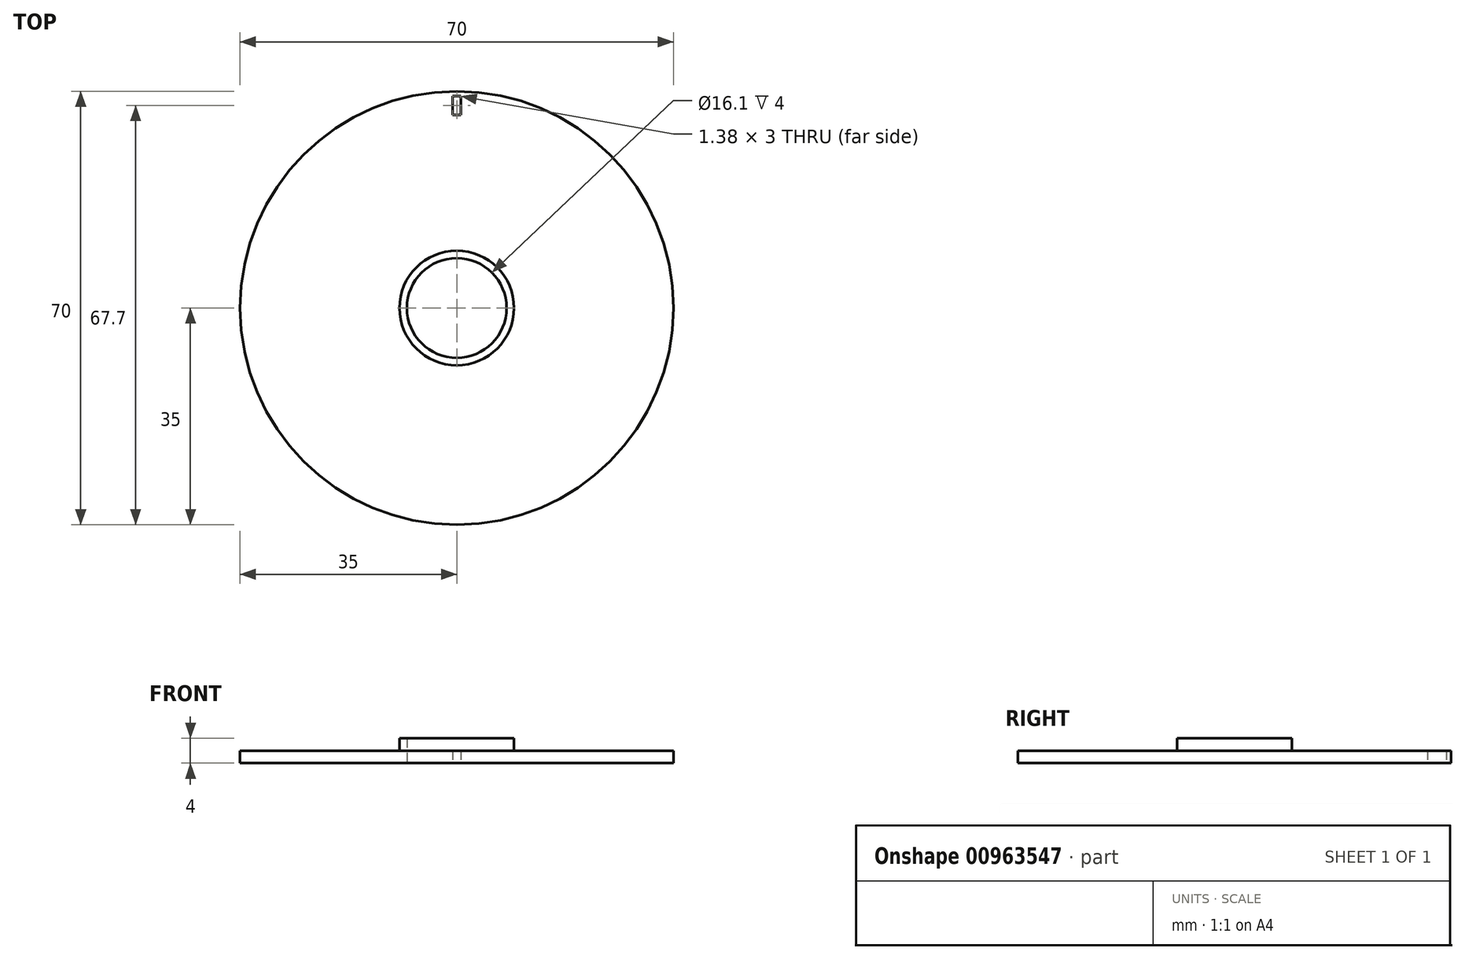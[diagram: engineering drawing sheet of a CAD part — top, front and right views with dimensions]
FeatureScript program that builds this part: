
annotation { "Feature Type Name" : "Feature", "Feature Type Description" : "" }
export const myFeature = defineFeature(function(context is Context, id is Id, definition is map)
    precondition{}
    {
        {
            var Q0;
            Q0=qCreatedBy(makeId("Top.planeOp"),FACE);
            var sketch = newSketch(context, id + "F0", { "sketchPlane" : qUnion([Q0])});
            skCircle(sketch, "E0", {"center": v(0, 0) * mm, "radius": 35 * mm});
            skSolve(sketch);
        }
        {
            var Q0;
            Q0=makeQuery(id+"F0.imprint","IMPRINT",FACE,{"disambiguationData":[TD([[makeQuery(id+"F0.imprint","IMPRINT",EDGE,{"derivedFrom":sQuery(id+"F0.wireOp",EDGE,"E0")}),1.0]])]});
            var sketch = newSketch(context, id + "F1", { "sketchPlane" : qUnion([Q0])});
            skLineSegment(sketch, "E1.bottom", {"start": v(0.69, 34.2) * mm, "end": v(-0.69, 34.2) * mm});
            skLineSegment(sketch, "E1.top", {"start": v(0.69, 31.2) * mm, "end": v(-0.69, 31.2) * mm});
            skLineSegment(sketch, "E1.left", {"start": v(0.69, 34.2) * mm, "end": v(0.69, 31.2) * mm});
            skLineSegment(sketch, "E1.right", {"start": v(-0.69, 34.2) * mm, "end": v(-0.69, 31.2) * mm});
            skPoint(sketch, "E1.middle", {"position": v(0, 32.7) * mm});
            skPoint(sketch, "E2", {"position": v(0, 0) * mm});
            skSolve(sketch);
        }
        {
            var Q0;
            Q0 = qSketchRegion(id + "F0", true);
            extrude(context, id + "F2", {"entities" : qUnion([Q0]), "depth" : 2 * mm, "offsetDistance" : 25 * mm});
        }
        {
            var Q0;
            Q0 = qSketchRegion(id + "F1", true);
            extrude(context, id + "F3", {"entities" : qUnion([Q0]), "operationType" : NewBodyOperationType.REMOVE, "endBound" : BoundingType.THROUGH_ALL, "depth" : 25 * mm, "offsetDistance" : 25 * mm});
        }
        {
            var Q0;
            Q0=sQuery(id+"F1.wireOp",VERTEX,"E2");
            var Q1;
            Q1=makeQuery(id+"F2.opExtrude","SWEPT_BODY",BODY,{"disambiguationData":[OSD([sQuery(id+"F0.wireOp",EDGE,"E0")])]});
            hole(context, id + "F4", {"style" : HoleStyle.SIMPLE, "endStyle" : HoleEndStyle.THROUGH, "oppositeDirection" : true, "holeDiameter" : 16.1 * mm, "majorDiameter" : 5 * mm, "isTappedThrough" : true, "tappedDepth" : 12 * mm, "tapClearance" : 3, "locations" : qUnion([Q0]), "scope" : qUnion([Q1])});
        }
        {
            var Q0;
            Q0=makeQuery(id+"F2.opExtrude","CAP_FACE",FACE,{"disambiguationData":[OSD([sQuery(id+"F0.wireOp",EDGE,"E0")])],"isStart":false});
            var sketch = newSketch(context, id + "F5", { "sketchPlane" : qUnion([Q0])});
            skCircle(sketch, "E3", {"center": v(0, 0) * mm, "radius": 9.25 * mm});
            skSolve(sketch);
        }
        {
            var Q0;
            Q0=makeQuery(id+"F5.imprint","IMPRINT",FACE,{"disambiguationData":[TD([[makeQuery(id+"F5.imprint","IMPRINT",EDGE,{"derivedFrom":sQuery(id+"F5.wireOp",EDGE,"E3")}),1.0]])]});
            extrude(context, id + "F6", {"entities" : qUnion([Q0]), "operationType" : NewBodyOperationType.ADD, "depth" : 2 * mm, "offsetDistance" : 25 * mm});
        }
    });
